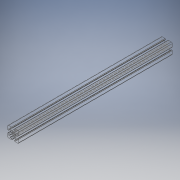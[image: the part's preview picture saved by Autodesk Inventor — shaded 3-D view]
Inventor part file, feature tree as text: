
AUTODESK INVENTOR PART (.ipt)
format: ipt  version: 2019 (Build 230136000, 136)  size: 233,472 bytes
history: native  units: in
note: dims shown in document units (in); Inventor stores cm internally (conversion verified against a paired STEP export)
features: plane x1, extrude x1, sketch x1
ambient origin geometry x8: Origin, YZ Plane, XZ Plane, XY Plane, X Axis, Y Axis, Z Axis, Center Point
bodies: Solid1 (feature_tree)
feature tree (3):
  plane  "Work Plane1"
  extrude  "Extrusion1"  [1 undecoded]
  sketch  "Sketch1"  dims[d0=21.0in d1=0.0in]
note: 1 required parameter value undecoded (feature->parameter linkage not recoverable at this tier; creation-order binding heuristic only, values carry confidence <= 0.55)
